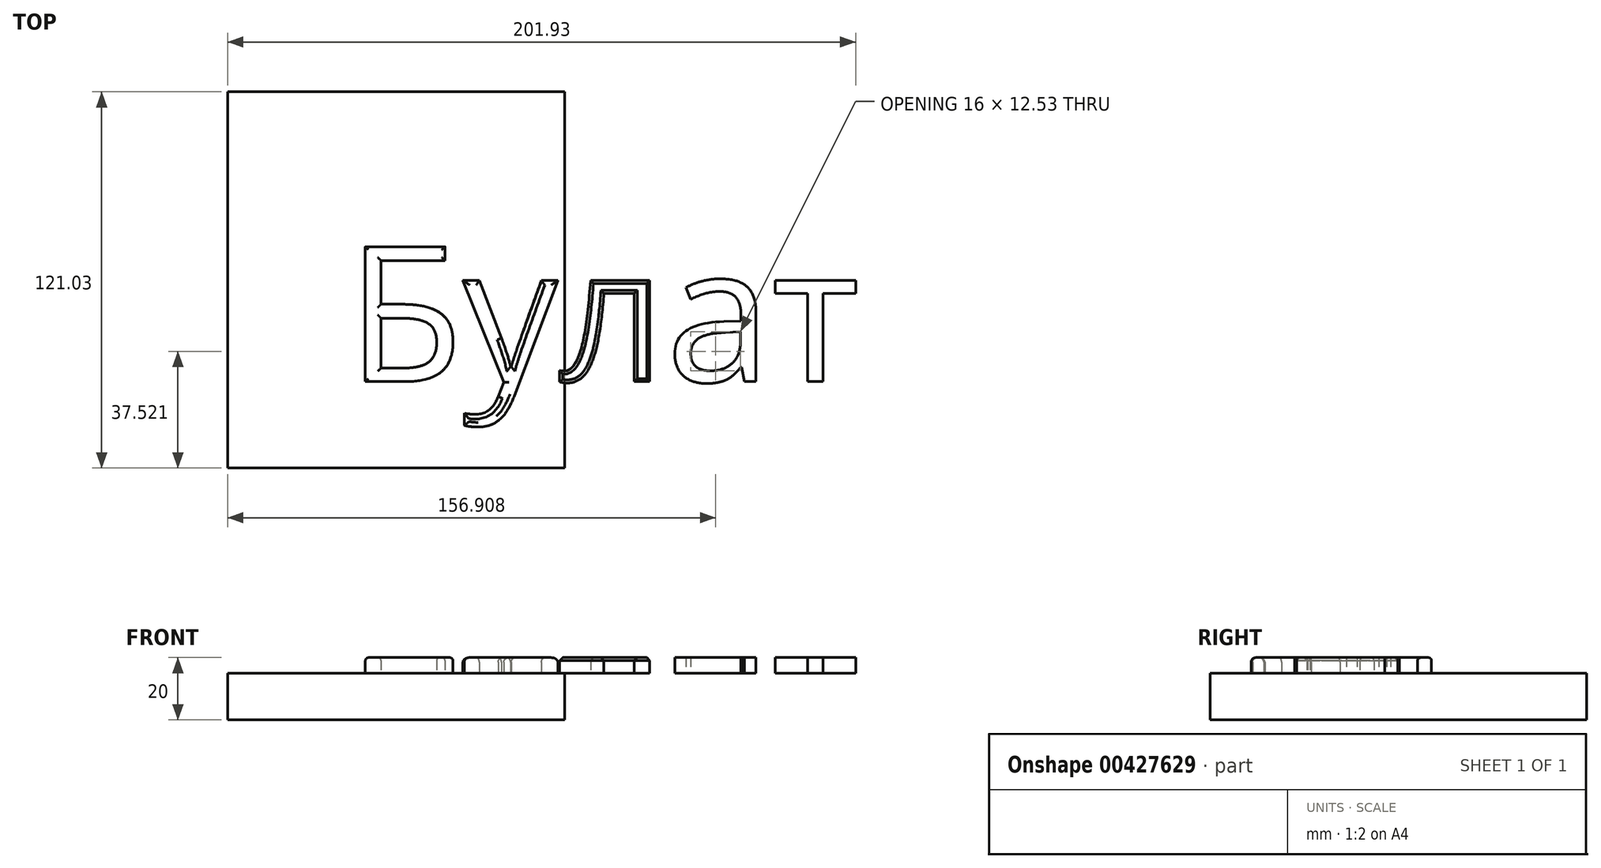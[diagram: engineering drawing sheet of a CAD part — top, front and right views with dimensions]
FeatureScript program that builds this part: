
annotation { "Feature Type Name" : "Feature", "Feature Type Description" : "" }
export const myFeature = defineFeature(function(context is Context, id is Id, definition is map)
    precondition{}
    {
        {
            var Q0;
            Q0=qCreatedBy(makeId("Top.planeOp"),FACE);
            var sketch = newSketch(context, id + "F0", { "sketchPlane" : qUnion([Q0])});
            skLineSegment(sketch, "E0.bottom", {"start": v(22.52, -33.47) * mm, "end": v(-85.85, -33.47) * mm});
            skLineSegment(sketch, "E0.top", {"start": v(22.52, 87.56) * mm, "end": v(-85.85, 87.56) * mm});
            skLineSegment(sketch, "E0.left", {"start": v(22.52, -33.47) * mm, "end": v(22.52, 87.56) * mm});
            skLineSegment(sketch, "E0.right", {"start": v(-85.85, -33.47) * mm, "end": v(-85.85, 87.56) * mm});
            skSolve(sketch);
        }
        {
            var Q0;
            Q0=makeQuery(id+"F0.imprint","IMPRINT",FACE,{"disambiguationData":[TD([[makeQuery(id+"F0.imprint","IMPRINT",EDGE,{"derivedFrom":sQuery(id+"F0.wireOp",EDGE,"E0.bottom")}),-1.0]])]});
            extrude(context, id + "F1", {"entities" : qUnion([Q0]), "depth" : 15 * mm});
        }
        {
            var Q0;
            Q0=makeQuery(id+"F1.opExtrude","CAP_FACE",FACE,{"disambiguationData":[OSD([sQuery(id+"F0.wireOp",EDGE,"E0.bottom"),sQuery(id+"F0.wireOp",EDGE,"E0.top"),sQuery(id+"F0.wireOp",EDGE,"E0.left"),sQuery(id+"F0.wireOp",EDGE,"E0.right")])],"isStart":false});
            var sketch = newSketch(context, id + "F2", { "sketchPlane" : qUnion([Q0])});
            skText(sketch, "E1", { "text": "Булат", "fontName": "OpenSans-Regular.ttf"});
            const initialGuessF2  = {"E1": [-0.04754, -0.00569, 1, 0, 0.04379]};
            skSetInitialGuess(sketch, initialGuessF2);
            skSolve(sketch);
        }
        {
            var Q0;
            Q0 = qSketchRegion(id + "F2", true);
            var Q1;
            Q1=makeQuery(id+"F2.imprint","IMPRINT",FACE,{"disambiguationData":[TD([[makeQuery(id+"F2.imprint","IMPRINT",EDGE,{"derivedFrom":sQuery(id+"F2.wireOp",EDGE,"E1.sketch_text.stroke-75")}),-1.0]])]});
            extrude(context, id + "F3", {"entities" : qUnion([Q0, Q1]), "operationType" : NewBodyOperationType.ADD, "depth" : 5 * mm});
        }
        {
            var Q0;
            Q0=makeQuery(id+"F3.opExtrude","CAP_FACE",FACE,{"disambiguationData":[OSD([sQuery(id+"F2.wireOp",EDGE,"E1.sketch_text.stroke-0"),sQuery(id+"F2.wireOp",EDGE,"E1.sketch_text.stroke-1"),sQuery(id+"F2.wireOp",EDGE,"E1.sketch_text.stroke-2"),sQuery(id+"F2.wireOp",EDGE,"E1.sketch_text.stroke-3"),sQuery(id+"F2.wireOp",EDGE,"E1.sketch_text.stroke-4"),sQuery(id+"F2.wireOp",EDGE,"E1.sketch_text.stroke-5"),sQuery(id+"F2.wireOp",EDGE,"E1.sketch_text.stroke-6"),sQuery(id+"F2.wireOp",EDGE,"E1.sketch_text.stroke-7"),sQuery(id+"F2.wireOp",EDGE,"E1.sketch_text.stroke-8"),sQuery(id+"F2.wireOp",EDGE,"E1.sketch_text.stroke-9"),sQuery(id+"F2.wireOp",EDGE,"E1.sketch_text.stroke-10"),sQuery(id+"F2.wireOp",EDGE,"E1.sketch_text.stroke-11"),sQuery(id+"F2.wireOp",EDGE,"E1.sketch_text.stroke-12"),sQuery(id+"F2.wireOp",EDGE,"E1.sketch_text.stroke-13"),sQuery(id+"F2.wireOp",EDGE,"E1.sketch_text.stroke-14"),sQuery(id+"F2.wireOp",EDGE,"E1.sketch_text.stroke-15"),sQuery(id+"F2.wireOp",EDGE,"E1.sketch_text.stroke-16"),sQuery(id+"F2.wireOp",EDGE,"E1.sketch_text.stroke-17"),sQuery(id+"F2.wireOp",EDGE,"E1.sketch_text.stroke-18")])],"isStart":false});
            fillet(context, id + "F4", {"entities" : qUnion([Q0]), "radius" : 1 * mm, "tangentPropagation" : true, "allowEdgeOverflow" : false});
        }
        {
            var Q0;
            Q0=makeQuery(id+"F3.opExtrude","CAP_FACE",FACE,{"disambiguationData":[OSD([sQuery(id+"F2.wireOp",EDGE,"E1.sketch_text.stroke-19"),sQuery(id+"F2.wireOp",EDGE,"E1.sketch_text.stroke-20"),sQuery(id+"F2.wireOp",EDGE,"E1.sketch_text.stroke-21"),sQuery(id+"F2.wireOp",EDGE,"E1.sketch_text.stroke-22"),sQuery(id+"F2.wireOp",EDGE,"E1.sketch_text.stroke-23"),sQuery(id+"F2.wireOp",EDGE,"E1.sketch_text.stroke-24"),sQuery(id+"F2.wireOp",EDGE,"E1.sketch_text.stroke-25"),sQuery(id+"F2.wireOp",EDGE,"E1.sketch_text.stroke-26"),sQuery(id+"F2.wireOp",EDGE,"E1.sketch_text.stroke-27"),sQuery(id+"F2.wireOp",EDGE,"E1.sketch_text.stroke-28"),sQuery(id+"F2.wireOp",EDGE,"E1.sketch_text.stroke-29"),sQuery(id+"F2.wireOp",EDGE,"E1.sketch_text.stroke-30"),sQuery(id+"F2.wireOp",EDGE,"E1.sketch_text.stroke-31"),sQuery(id+"F2.wireOp",EDGE,"E1.sketch_text.stroke-32"),sQuery(id+"F2.wireOp",EDGE,"E1.sketch_text.stroke-33"),sQuery(id+"F2.wireOp",EDGE,"E1.sketch_text.stroke-34")])],"isStart":false});
            fillet(context, id + "F5", {"entities" : qUnion([Q0]), "radius" : 1.5 * mm, "tangentPropagation" : true, "allowEdgeOverflow" : false});
        }
        {
            var Q0;
            Q0=makeQuery(id+"F3.opExtrude","CAP_EDGE",EDGE,{"disambiguationData":[OSD([sQuery(id+"F2.wireOp",EDGE,"E1.sketch_text.stroke-38")])],"isStart":false});
            var Q1;
            Q1=makeQuery(id+"F3.opExtrude","CAP_EDGE",EDGE,{"disambiguationData":[OSD([sQuery(id+"F2.wireOp",EDGE,"E1.sketch_text.stroke-44")])],"isStart":false});
            var Q2;
            Q2=makeQuery(id+"F3.opExtrude","CAP_FACE",FACE,{"disambiguationData":[OSD([sQuery(id+"F2.wireOp",EDGE,"E1.sketch_text.stroke-35"),sQuery(id+"F2.wireOp",EDGE,"E1.sketch_text.stroke-36"),sQuery(id+"F2.wireOp",EDGE,"E1.sketch_text.stroke-37"),sQuery(id+"F2.wireOp",EDGE,"E1.sketch_text.stroke-38"),sQuery(id+"F2.wireOp",EDGE,"E1.sketch_text.stroke-39"),sQuery(id+"F2.wireOp",EDGE,"E1.sketch_text.stroke-40"),sQuery(id+"F2.wireOp",EDGE,"E1.sketch_text.stroke-41"),sQuery(id+"F2.wireOp",EDGE,"E1.sketch_text.stroke-42"),sQuery(id+"F2.wireOp",EDGE,"E1.sketch_text.stroke-43"),sQuery(id+"F2.wireOp",EDGE,"E1.sketch_text.stroke-44"),sQuery(id+"F2.wireOp",EDGE,"E1.sketch_text.stroke-45"),sQuery(id+"F2.wireOp",EDGE,"E1.sketch_text.stroke-46"),sQuery(id+"F2.wireOp",EDGE,"E1.sketch_text.stroke-47")])],"isStart":false});
            chamfer(context, id + "F6", {"entities" : qUnion([Q0, Q1, Q2]), "width" : 1 * mm, "tangentPropagation" : true});
        }
    });
